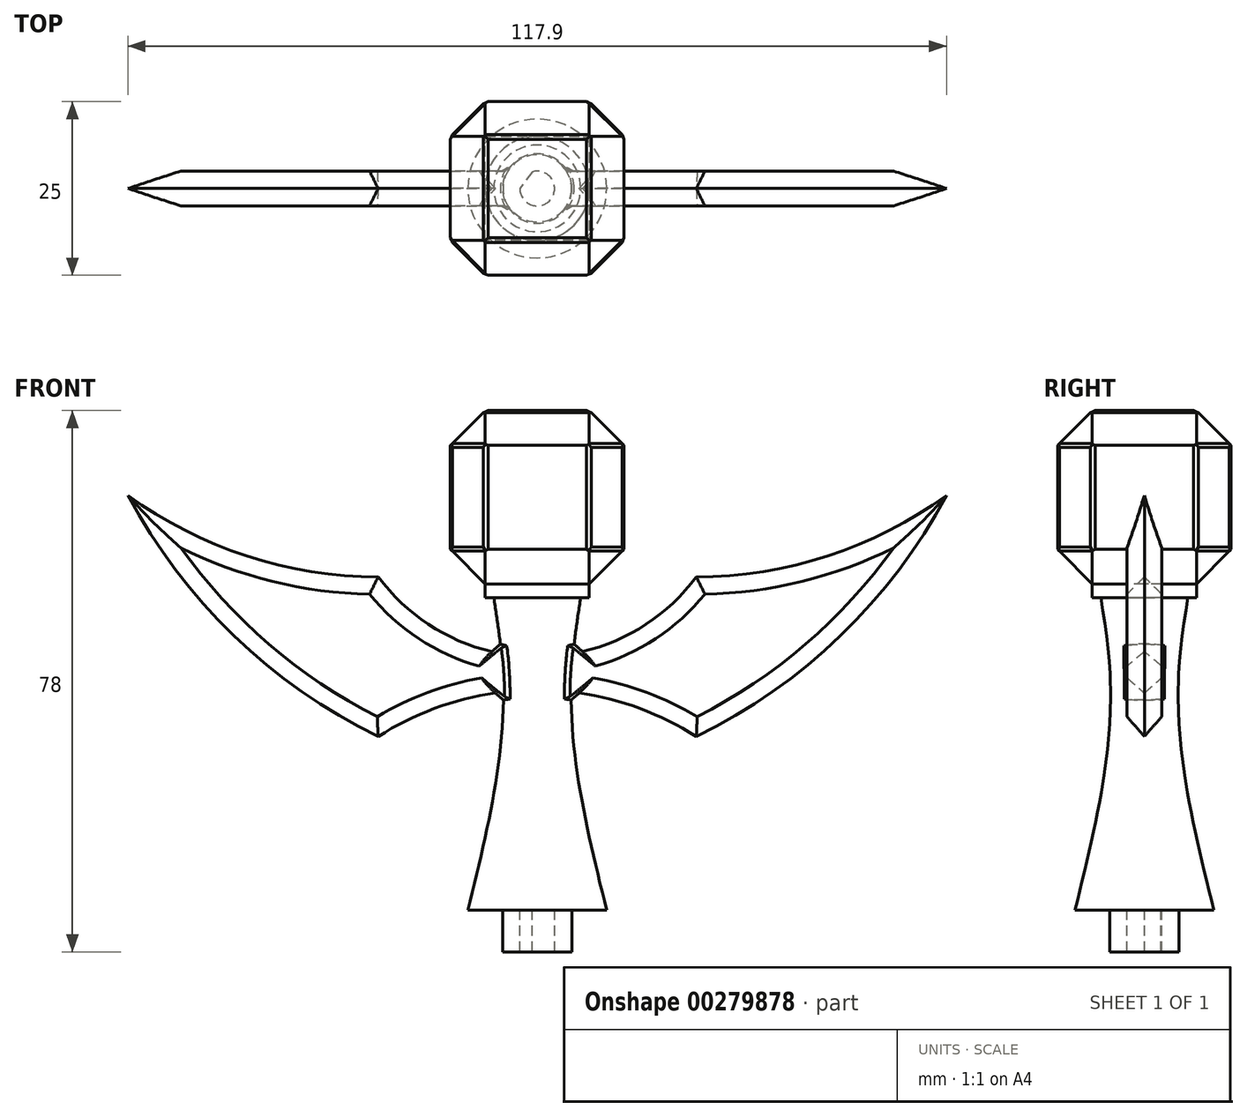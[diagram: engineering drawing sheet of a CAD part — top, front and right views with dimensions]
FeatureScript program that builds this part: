
annotation { "Feature Type Name" : "Feature", "Feature Type Description" : "" }
export const myFeature = defineFeature(function(context is Context, id is Id, definition is map)
    precondition{}
    {
        {
            var Q0;
            Q0=qCreatedBy(makeId("Top.planeOp"),FACE);
            cPlane(context, id + "F0", {"entities" : qUnion([Q0]), "cplaneType" : CPlaneType.OFFSET, "offset" : 35 * mm, "width" : 152.4 * mm, "height" : 152.4 * mm});
        }
        {
            var Q0;
            Q0=qCreatedBy(id+"F0.planeOp",FACE);
            cPlane(context, id + "F1", {"entities" : qUnion([Q0]), "cplaneType" : CPlaneType.OFFSET, "offset" : 10 * mm, "width" : 150 * mm, "height" : 150 * mm});
        }
        {
            var Q0;
            Q0=qCreatedBy(makeId("Top.planeOp"),FACE);
            var sketch = newSketch(context, id + "F2", { "sketchPlane" : qUnion([Q0])});
            skCircle(sketch, "E0", {"center": v(0, 0) * mm, "radius": 10 * mm});
            skSolve(sketch);
        }
        {
            var Q0;
            Q0=qCreatedBy(id+"F0.planeOp",FACE);
            var sketch = newSketch(context, id + "F3", { "sketchPlane" : qUnion([Q0])});
            skCircle(sketch, "E1", {"center": v(0, 0) * mm, "radius": 5 * mm});
            skSolve(sketch);
        }
        {
            var Q0;
            Q0=qCreatedBy(id+"F1.planeOp",FACE);
            var sketch = newSketch(context, id + "F4", { "sketchPlane" : qUnion([Q0])});
            skCircle(sketch, "E2", {"center": v(0, 0) * mm, "radius": 6.25 * mm});
            skSolve(sketch);
        }
        {
            var Q0;
            Q0=makeQuery(id+"F2.imprint","IMPRINT",FACE,{"disambiguationData":[TD([[makeQuery(id+"F2.imprint","IMPRINT",EDGE,{"derivedFrom":sQuery(id+"F2.wireOp",EDGE,"E0")}),1.0]])]});
            var Q1;
            Q1=makeQuery(id+"F3.imprint","IMPRINT",FACE,{"disambiguationData":[TD([[makeQuery(id+"F3.imprint","IMPRINT",EDGE,{"derivedFrom":sQuery(id+"F3.wireOp",EDGE,"E1")}),1.0]])]});
            var Q2;
            Q2=makeQuery(id+"F4.imprint","IMPRINT",FACE,{"disambiguationData":[TD([[makeQuery(id+"F4.imprint","IMPRINT",EDGE,{"derivedFrom":sQuery(id+"F4.wireOp",EDGE,"E2")}),1.0]])]});
            loft(context, id + "F5", {"sheetProfilesArray" : [{ "sheetProfileEntities" : qUnion([Q0]) }, { "sheetProfileEntities" : qUnion([Q1]) }, { "sheetProfileEntities" : qUnion([Q2]) }]});
        }
        {
            var Q0;
            Q0=makeQuery(id+"F5.opLoft","CAP_FACE",FACE,{"disambiguationData":[OSD([makeQuery(id+"F4.imprint","IMPRINT",FACE,{"disambiguationData":[TD([[makeQuery(id+"F4.imprint","IMPRINT",EDGE,{"derivedFrom":sQuery(id+"F4.wireOp",EDGE,"E2")}),1.0]])]})])],"isStart":true});
            var sketch = newSketch(context, id + "F6", { "sketchPlane" : qUnion([Q0])});
            skCircle(sketch, "E3", {"center": v(0, 0) * mm, "radius": 7.5 * mm});
            skSolve(sketch);
        }
        {
            var Q0;
            Q0 = qSketchRegion(id + "F6", true);
            extrude(context, id + "F7", {"entities" : qUnion([Q0]), "operationType" : NewBodyOperationType.ADD, "depth" : 2 * mm});
        }
        {
            var Q0;
            Q0=qCreatedBy(makeId("Front.planeOp"),FACE);
            var sketch = newSketch(context, id + "F8", { "sketchPlane" : qUnion([Q0])});
            skLineSegment(sketch, "E4.bottom", {"start": v(12.5, 72) * mm, "end": v(-12.5, 72) * mm});
            skLineSegment(sketch, "E4.top", {"start": v(12.5, 47) * mm, "end": v(-12.5, 47) * mm});
            skLineSegment(sketch, "E4.left", {"start": v(12.5, 72) * mm, "end": v(12.5, 47) * mm});
            skLineSegment(sketch, "E4.right", {"start": v(-12.5, 72) * mm, "end": v(-12.5, 47) * mm});
            skPoint(sketch, "E4.middle", {"position": v(0, 59.5) * mm});
            skSolve(sketch);
        }
        {
            var Q0;
            Q0 = qSketchRegion(id + "F8", true);
            extrude(context, id + "F9", {"entities" : qUnion([Q0]), "operationType" : NewBodyOperationType.ADD, "depth" : 12.5 * mm, "hasSecondDirection" : true, "secondDirectionOppositeDirection" : true, "secondDirectionDepth" : 12.5 * mm});
        }
        {
            var Q0;
            Q0=makeQuery(id+"F9.opExtrude","CAP_FACE",FACE,{"disambiguationData":[OSD([sQuery(id+"F8.wireOp",EDGE,"E4.bottom"),sQuery(id+"F8.wireOp",EDGE,"E4.top"),sQuery(id+"F8.wireOp",EDGE,"E4.left"),sQuery(id+"F8.wireOp",EDGE,"E4.right")])],"isStart":true});
            var Q1;
            Q1=makeQuery(id+"F9.opExtrude","SWEPT_FACE",FACE,{"disambiguationData":[OSD([sQuery(id+"F8.wireOp",EDGE,"E4.left")])]});
            var Q2;
            Q2=makeQuery(id+"F9.opExtrude","SWEPT_FACE",FACE,{"disambiguationData":[OSD([sQuery(id+"F8.wireOp",EDGE,"E4.bottom")])]});
            var Q3;
            Q3=makeQuery(id+"F9.opExtrude","CAP_FACE",FACE,{"disambiguationData":[OSD([sQuery(id+"F8.wireOp",EDGE,"E4.bottom"),sQuery(id+"F8.wireOp",EDGE,"E4.top"),sQuery(id+"F8.wireOp",EDGE,"E4.left"),sQuery(id+"F8.wireOp",EDGE,"E4.right")])],"isStart":false});
            var Q4;
            Q4=makeQuery(id+"F9.opExtrude","SWEPT_FACE",FACE,{"disambiguationData":[OSD([sQuery(id+"F8.wireOp",EDGE,"E4.right")])]});
            chamfer(context, id + "F10", {"entities" : qUnion([Q0, Q1, Q2, Q3, Q4]), "width" : 5 * mm, "tangentPropagation" : true});
        }
        {
            var Q0;
            {var subQ0=sQuery(id+"F8.wireOp",EDGE,"E4.right");Q0=makeQuery(id+"F10.opChamfer","BLEND_FACE",FACE,{"disambiguationData":[OSD([subQ0]),TDD([makeQuery(id+"F9.opExtrude","CAP_EDGE",EDGE,{"disambiguationData":[OSD([subQ0])],"isStart":false})])]});}
            var Q1;
            {var subQ0=sQuery(id+"F8.wireOp",EDGE,"E4.left");Q1=makeQuery(id+"F10.opChamfer","BLEND_FACE",FACE,{"disambiguationData":[OSD([subQ0]),TDD([makeQuery(id+"F9.opExtrude","CAP_EDGE",EDGE,{"disambiguationData":[OSD([subQ0])],"isStart":false})])]});}
            var Q2;
            Q2=makeQuery(id+"F9.opExtrude","SWEPT_FACE",FACE,{"disambiguationData":[OSD([sQuery(id+"F8.wireOp",EDGE,"E4.bottom")])]});
            var Q3;
            {var subQ0=sQuery(id+"F8.wireOp",EDGE,"E4.left");Q3=makeQuery(id+"F10.opChamfer","BLEND_FACE",FACE,{"disambiguationData":[OSD([subQ0]),TDD([makeQuery(id+"F9.opExtrude","CAP_EDGE",EDGE,{"disambiguationData":[OSD([subQ0])],"isStart":true})])]});}
            var Q4;
            {var subQ0=sQuery(id+"F8.wireOp",EDGE,"E4.right");Q4=makeQuery(id+"F10.opChamfer","BLEND_FACE",FACE,{"disambiguationData":[OSD([subQ0]),TDD([makeQuery(id+"F9.opExtrude","CAP_EDGE",EDGE,{"disambiguationData":[OSD([subQ0])],"isStart":true})])]});}
            chamfer(context, id + "F11", {"entities" : qUnion([Q0, Q1, Q2, Q3, Q4]), "width" : 1 * mm, "tangentPropagation" : true});
        }
        {
            var Q0;
            Q0=qCreatedBy(makeId("Front.planeOp"),FACE);
            var sketch = newSketch(context, id + "F12", { "sketchPlane" : qUnion([Q0])});
            skArc(sketch, "E5", {"start": v(-22.9, 48.03) * mm, "mid": v(-12.82, 39.55) * mm, "end": v(0, 36.5) * mm});
            skLineSegment(sketch, "E6", {"start": v(0, 36.5) * mm, "end": v(15.76, 36.5) * mm, "construction": true});
            skArc(sketch, "E7", {"start": v(-58.95, 59.78) * mm, "mid": v(-41.86, 51.04) * mm, "end": v(-22.9, 48.03) * mm});
            skLineSegment(sketch, "E8", {"start": v(-22.9, 48.03) * mm, "end": v(0, 48.03) * mm, "construction": true});
            skArc(sketch, "E9", {"start": v(-58.95, 59.78) * mm, "mid": v(-43.68, 39.55) * mm, "end": v(-22.9, 25.03) * mm});
            skArc(sketch, "E10", {"start": v(0, 31.71) * mm, "mid": v(-11.93, 30) * mm, "end": v(-22.9, 25.03) * mm});
            skLineSegment(sketch, "E11", {"start": v(0, 31.71) * mm, "end": v(20.42, 31.71) * mm, "construction": true});
            skLineSegment(sketch, "E12", {"start": v(-22.9, 48.03) * mm, "end": v(-22.9, 25.03) * mm, "construction": true});
            skLineSegment(sketch, "E13", {"start": v(0, 36.5) * mm, "end": v(0, 31.71) * mm});
            skSolve(sketch);
        }
        {
            var Q0;
            Q0 = qSketchRegion(id + "F12", true);
            extrude(context, id + "F13", {"entities" : qUnion([Q0]), "operationType" : NewBodyOperationType.ADD, "depth" : 2.5 * mm, "hasSecondDirection" : true, "secondDirectionOppositeDirection" : true, "secondDirectionDepth" : 2.5 * mm});
        }
        {
            var Q0;
            Q0=makeQuery(id+"F13.boolean.opBoolean","INTERSECT",EDGE,{"derivedFrom":[makeQuery(id+"F5.opLoft","SWEPT_FACE",FACE,{"disambiguationData":[OSD([sQuery(id+"F2.wireOp",EDGE,"E0"),sQuery(id+"F3.wireOp",EDGE,"E1")])]}),makeQuery(id+"F13.opExtrude","CAP_FACE",FACE,{"disambiguationData":[OSD([sQuery(id+"F12.wireOp",EDGE,"E5"),sQuery(id+"F12.wireOp",EDGE,"E7"),sQuery(id+"F12.wireOp",EDGE,"E9"),sQuery(id+"F12.wireOp",EDGE,"E10"),sQuery(id+"F12.wireOp",EDGE,"E13")])],"isStart":true})]});
            var Q1;
            Q1=makeQuery(id+"F13.boolean.opBoolean","INTERSECT",EDGE,{"derivedFrom":[makeQuery(id+"F5.opLoft","SWEPT_FACE",FACE,{"disambiguationData":[OSD([sQuery(id+"F2.wireOp",EDGE,"E0"),sQuery(id+"F3.wireOp",EDGE,"E1")])]}),makeQuery(id+"F13.opExtrude","CAP_FACE",FACE,{"disambiguationData":[OSD([sQuery(id+"F12.wireOp",EDGE,"E5"),sQuery(id+"F12.wireOp",EDGE,"E7"),sQuery(id+"F12.wireOp",EDGE,"E9"),sQuery(id+"F12.wireOp",EDGE,"E10"),sQuery(id+"F12.wireOp",EDGE,"E13")])],"isStart":false})]});
            var Q2;
            Q2=makeQuery(id+"F13.boolean.opBoolean","INTERSECT",EDGE,{"derivedFrom":[makeQuery(id+"F5.opLoft","SWEPT_FACE",FACE,{"disambiguationData":[OSD([sQuery(id+"F2.wireOp",EDGE,"E0"),sQuery(id+"F3.wireOp",EDGE,"E1")])]}),makeQuery(id+"F13.opExtrude","SWEPT_FACE",FACE,{"disambiguationData":[OSD([sQuery(id+"F12.wireOp",EDGE,"E5")])]})]});
            var Q3;
            Q3=makeQuery(id+"F13.boolean.opBoolean","INTERSECT",EDGE,{"derivedFrom":[makeQuery(id+"F5.opLoft","SWEPT_FACE",FACE,{"disambiguationData":[OSD([sQuery(id+"F2.wireOp",EDGE,"E0"),sQuery(id+"F3.wireOp",EDGE,"E1")])]}),makeQuery(id+"F13.opExtrude","SWEPT_FACE",FACE,{"disambiguationData":[OSD([sQuery(id+"F12.wireOp",EDGE,"E10")])]})]});
            chamfer(context, id + "F14", {"entities" : qUnion([Q0, Q1, Q2, Q3]), "width" : 1 * mm, "tangentPropagation" : true});
        }
        {
            var Q0;
            Q0=makeQuery(id+"F13.opExtrude","CAP_EDGE",EDGE,{"disambiguationData":[OSD([sQuery(id+"F12.wireOp",EDGE,"E5")])],"isStart":true});
            var Q1;
            Q1=makeQuery(id+"F13.opExtrude","CAP_EDGE",EDGE,{"disambiguationData":[OSD([sQuery(id+"F12.wireOp",EDGE,"E7")])],"isStart":true});
            var Q2;
            Q2=makeQuery(id+"F13.opExtrude","CAP_EDGE",EDGE,{"disambiguationData":[OSD([sQuery(id+"F12.wireOp",EDGE,"E9")])],"isStart":true});
            var Q3;
            Q3=makeQuery(id+"F13.opExtrude","CAP_EDGE",EDGE,{"disambiguationData":[OSD([sQuery(id+"F12.wireOp",EDGE,"E7")])],"isStart":false});
            var Q4;
            Q4=makeQuery(id+"F13.opExtrude","CAP_EDGE",EDGE,{"disambiguationData":[OSD([sQuery(id+"F12.wireOp",EDGE,"E5")])],"isStart":false});
            var Q5;
            Q5=makeQuery(id+"F13.opExtrude","CAP_EDGE",EDGE,{"disambiguationData":[OSD([sQuery(id+"F12.wireOp",EDGE,"E9")])],"isStart":false});
            var Q6;
            Q6=makeQuery(id+"F13.opExtrude","CAP_EDGE",EDGE,{"disambiguationData":[OSD([sQuery(id+"F12.wireOp",EDGE,"E10")])],"isStart":false});
            var Q7;
            Q7=makeQuery(id+"F13.opExtrude","CAP_EDGE",EDGE,{"disambiguationData":[OSD([sQuery(id+"F12.wireOp",EDGE,"E10")])],"isStart":true});
            chamfer(context, id + "F15", {"entities" : qUnion([Q0, Q1, Q2, Q3, Q4, Q5, Q6, Q7]), "width" : 2.5 * mm, "tangentPropagation" : true});
        }
        {
            var Q0;
            Q0=makeQuery(id+"F5.opLoft","SWEPT_BODY",BODY,{"disambiguationData":[OSD([makeQuery(id+"F2.imprint","IMPRINT",FACE,{"disambiguationData":[TD([[makeQuery(id+"F2.imprint","IMPRINT",EDGE,{"derivedFrom":sQuery(id+"F2.wireOp",EDGE,"E0")}),1.0]])]}),sQuery(id+"F3.wireOp",EDGE,"E1"),makeQuery(id+"F4.imprint","IMPRINT",FACE,{"disambiguationData":[TD([[makeQuery(id+"F4.imprint","IMPRINT",EDGE,{"derivedFrom":sQuery(id+"F4.wireOp",EDGE,"E2")}),1.0]])]})])]});
            var Q1;
            Q1=qCreatedBy(makeId("Right.planeOp"),FACE);
            mirror(context, id + "F16", {"operationType" : NewBodyOperationType.ADD, "entities" : qUnion([Q0]), "mirrorPlane" : qUnion([Q1])});
        }
        {
            var Q0;
            Q0=makeQuery(id+"F5.opLoft","CAP_FACE",FACE,{"disambiguationData":[OSD([makeQuery(id+"F2.imprint","IMPRINT",FACE,{"disambiguationData":[TD([[makeQuery(id+"F2.imprint","IMPRINT",EDGE,{"derivedFrom":sQuery(id+"F2.wireOp",EDGE,"E0")}),1.0]])]})])],"isStart":true});
            var sketch = newSketch(context, id + "F17", { "sketchPlane" : qUnion([Q0])});
            skCircle(sketch, "E14", {"center": v(0, 0) * mm, "radius": 2.5 * mm});
            skLineSegment(sketch, "E15", {"start": v(-0.7, -2.4) * mm, "end": v(-2.5, 0) * mm});
            skLineSegment(sketch, "E16", {"start": v(-1.6, -1.2) * mm, "end": v(2, 1.5) * mm});
            skCircle(sketch, "E17", {"center": v(0, 0) * mm, "radius": 5 * mm});
            skSolve(sketch);
        }
        {
            var Q0;
            Q0 = qSketchRegion(id + "F17", true);
            var Q1;
            {var subQ0=sQuery(id+"F17.wireOp",EDGE,"E15");var subQ1=sQuery(id+"F17.wireOp",EDGE,"E14");var subQ2=makeQuery(id+"F17.imprint","INTERSECT",VERTEX,{"disambiguationData":[OD(0.0)],"derivedFrom":[subQ1,subQ0]});Q1=makeQuery(id+"F17.imprint","IMPRINT",FACE,{"disambiguationData":[TD([[makeQuery(id+"F17.imprint","IMPRINT",EDGE,{"disambiguationData":[TD([[subQ2,1.0]])],"derivedFrom":subQ1}),1.0]])]});}
            extrude(context, id + "F18", {"entities" : qUnion([Q0, Q1]), "operationType" : NewBodyOperationType.ADD, "depth" : 6 * mm});
        }
    });
